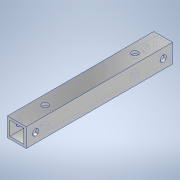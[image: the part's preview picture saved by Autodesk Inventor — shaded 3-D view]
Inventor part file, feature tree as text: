
AUTODESK INVENTOR PART (.ipt)
format: ipt  version: 2020.3 (Build 243373000, 373)  size: 129,024 bytes
history: native  units: mm
features: sketch x3, hole x2, other x1, extrude x1
ambient origin geometry x8: Origin, YZ Plane, XZ Plane, XY Plane, X Axis, Y Axis, Z Axis, Center Point
bodies: Body1 (feature_tree)
feature tree (7):
  other  "ソリッド1"
  extrude  "押し出し1"  Depth=9.0mm
  hole  "穴1"  [1 undecoded]
  hole  "穴2"  [1 undecoded]
  sketch  "スケッチ1"
  sketch  "スケッチ2"
  sketch  "スケッチ3"
note: 2 required parameter values undecoded (feature->parameter linkage not recoverable at this tier; creation-order binding heuristic only, values carry confidence <= 0.55)
